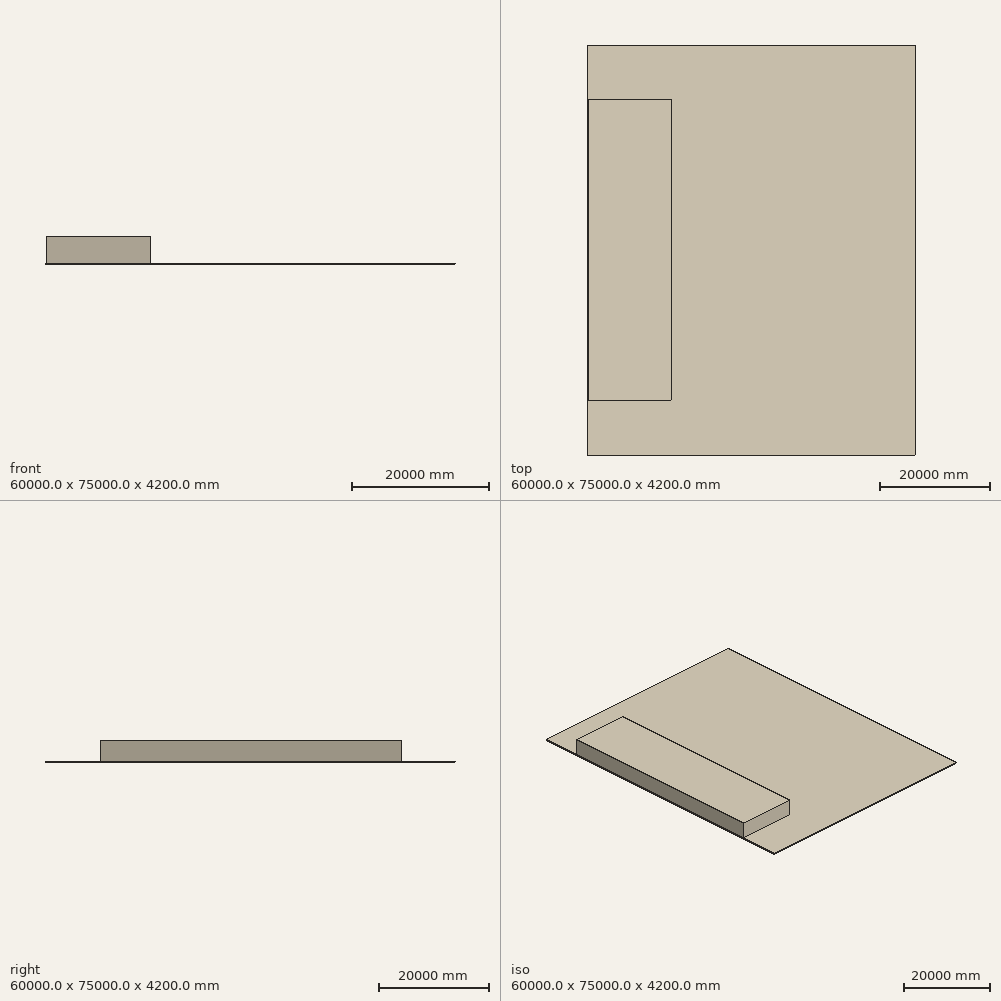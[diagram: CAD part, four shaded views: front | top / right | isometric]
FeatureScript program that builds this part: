
annotation { "Feature Type Name" : "Feature", "Feature Type Description" : "" }
export const myFeature = defineFeature(function(context is Context, id is Id, definition is map)
    precondition{}
    {
        {
            var Q0;
            Q0=qCreatedBy(makeId("Top.planeOp"),FACE);
            var sketch = newSketch(context, id + "F0", { "sketchPlane" : qUnion([Q0])});
            skLineSegment(sketch, "E0.bottom", {"start": v(-29840.16, 94766.37) * mm, "end": v(30159.84, 94766.37) * mm});
            skLineSegment(sketch, "E0.top", {"start": v(-29840.16, 19766.37) * mm, "end": v(30159.84, 19766.37) * mm});
            skLineSegment(sketch, "E0.left", {"start": v(-29840.16, 94766.37) * mm, "end": v(-29840.16, 19766.37) * mm});
            skLineSegment(sketch, "E0.right", {"start": v(30159.84, 94766.37) * mm, "end": v(30159.84, 19766.37) * mm});
            skLineSegment(sketch, "E1.bottom", {"start": v(-29740.16, 84916.37) * mm, "end": v(-14540.16, 84916.37) * mm});
            skLineSegment(sketch, "E1.top", {"start": v(-29740.16, 29916.37) * mm, "end": v(-14540.16, 29916.37) * mm});
            skLineSegment(sketch, "E1.left", {"start": v(-29740.16, 84916.37) * mm, "end": v(-29740.16, 29916.37) * mm});
            skLineSegment(sketch, "E1.right", {"start": v(-14540.16, 84916.37) * mm, "end": v(-14540.16, 29916.37) * mm});
            skSolve(sketch);
        }
        {
            var Q0;
            Q0=makeQuery(id+"F0.imprint","IMPRINT",FACE,{"disambiguationData":[TD([[makeQuery(id+"F0.imprint","IMPRINT",EDGE,{"derivedFrom":sQuery(id+"F0.wireOp",EDGE,"E1.bottom")}),-1.0]])]});
            extrude(context, id + "F1", {"entities" : qUnion([Q0]), "depth" : 4000 * mm});
        }
        {
            var Q0;
            Q0=makeQuery(id+"F0.imprint","IMPRINT",FACE,{"disambiguationData":[TD([[makeQuery(id+"F0.imprint","IMPRINT",EDGE,{"derivedFrom":sQuery(id+"F0.wireOp",EDGE,"E0.bottom")}),-1.0]])]});
            var Q1;
            Q1=makeQuery(id+"F0.imprint","IMPRINT",FACE,{"disambiguationData":[TD([[makeQuery(id+"F0.imprint","IMPRINT",EDGE,{"derivedFrom":sQuery(id+"F0.wireOp",EDGE,"E1.bottom")}),-1.0]])]});
            extrude(context, id + "F2", {"entities" : qUnion([Q0, Q1]), "operationType" : NewBodyOperationType.ADD, "oppositeDirection" : true, "depth" : 200 * mm});
        }
    });
